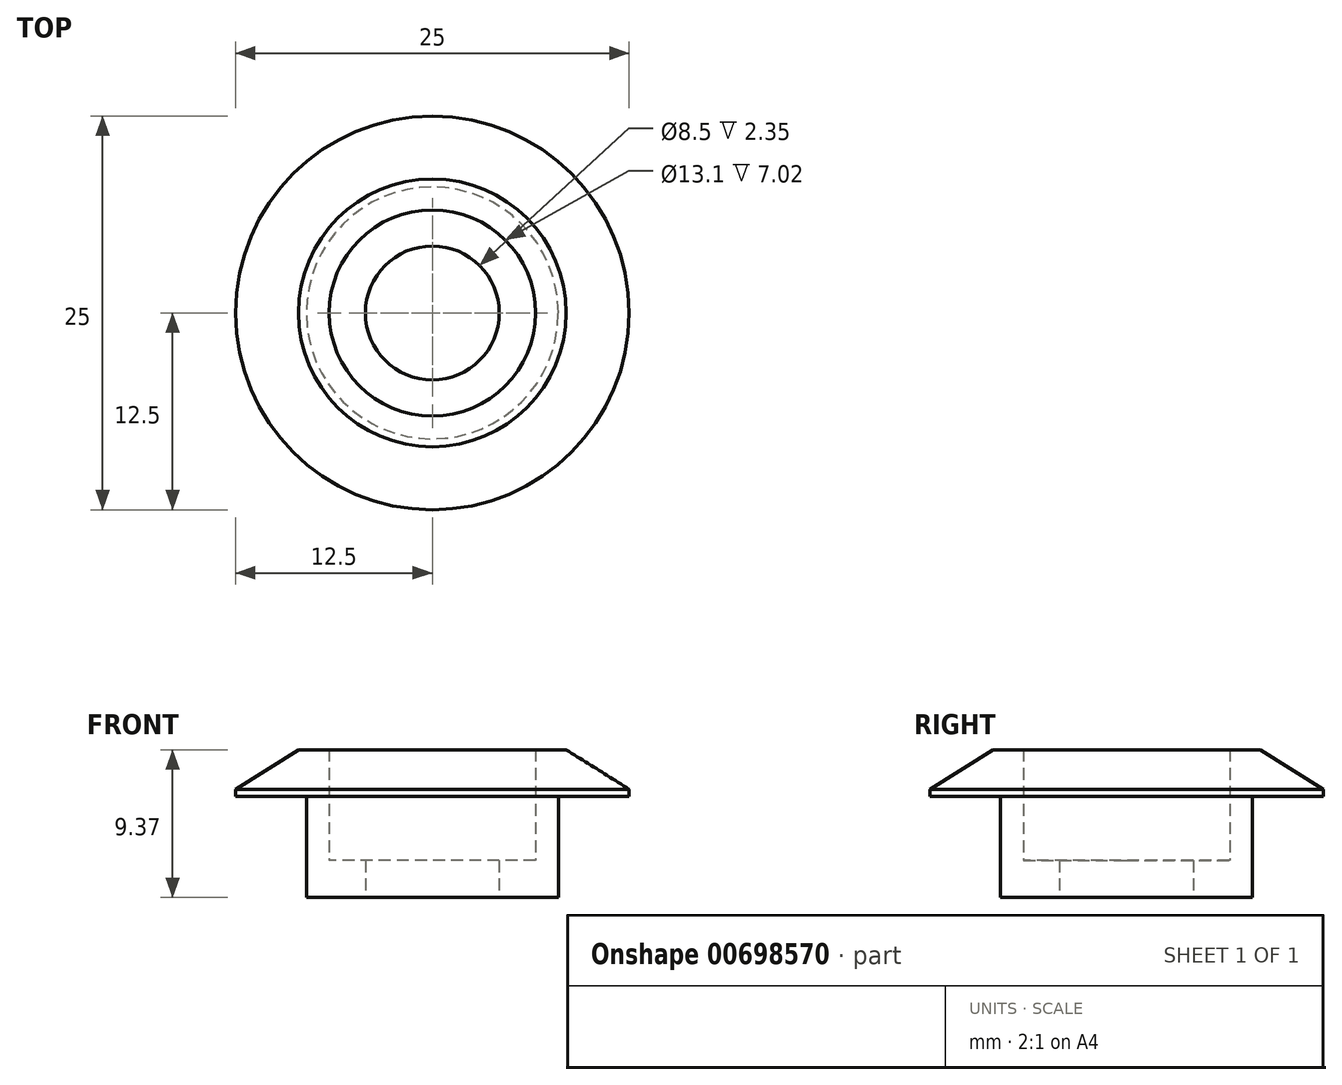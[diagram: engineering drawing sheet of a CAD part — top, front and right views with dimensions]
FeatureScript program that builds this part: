
annotation { "Feature Type Name" : "Feature", "Feature Type Description" : "" }
export const myFeature = defineFeature(function(context is Context, id is Id, definition is map)
    precondition{}
    {
        {
            var Q0;
            Q0=qCreatedBy(makeId("Top.planeOp"),FACE);
            var sketch = newSketch(context, id + "F0", { "sketchPlane" : qUnion([Q0])});
            skCircle(sketch, "E0", {"center": v(0, 0) * mm, "radius": 12.5 * mm});
            skSolve(sketch);
        }
        {
            var Q0;
            Q0 = qSketchRegion(id + "F0", true);
            extrude(context, id + "F1", {"entities" : qUnion([Q0]), "depth" : 9.37 * mm, "offsetDistance" : 25 * mm, "hasSecondDirection" : true, "secondDirectionOppositeDirection" : false, "secondDirectionDepth" : 6.4 * mm});
        }
        {
            var Q0;
            Q0=qCreatedBy(makeId("Top.planeOp"),FACE);
            var sketch = newSketch(context, id + "F2", { "sketchPlane" : qUnion([Q0])});
            skCircle(sketch, "E1", {"center": v(0, 0) * mm, "radius": 8 * mm});
            skSolve(sketch);
        }
        {
            var Q0;
            Q0 = qSketchRegion(id + "F2", true);
            extrude(context, id + "F3", {"entities" : qUnion([Q0]), "operationType" : NewBodyOperationType.ADD, "endBound" : BoundingType.UP_TO_NEXT, "depth" : 25 * mm, "offsetDistance" : 25 * mm});
        }
        {
            var Q0;
            Q0=makeQuery(id+"F1.opExtrude","CAP_EDGE",EDGE,{"disambiguationData":[OSD([sQuery(id+"F0.wireOp",EDGE,"E0")])],"isStart":false});
            chamfer(context, id + "F4", {"entities" : qUnion([Q0]), "chamferType" : ChamferType.TWO_OFFSETS, "width1" : 4 * mm, "oppositeDirection" : false, "width2" : 2.5 * mm, "tangentPropagation" : true});
        }
        {
            var Q0;
            Q0=qCreatedBy(makeId("Top.planeOp"),FACE);
            var sketch = newSketch(context, id + "F5", { "sketchPlane" : qUnion([Q0])});
            skCircle(sketch, "E2", {"center": v(0, 0) * mm, "radius": 4.25 * mm});
            skSolve(sketch);
        }
        {
            var Q0;
            Q0 = qSketchRegion(id + "F5", true);
            extrude(context, id + "F6", {"entities" : qUnion([Q0]), "operationType" : NewBodyOperationType.REMOVE, "endBound" : BoundingType.UP_TO_NEXT, "depth" : 25 * mm, "offsetDistance" : 25 * mm});
        }
        {
            var Q0;
            Q0=qCreatedBy(makeId("Top.planeOp"),FACE);
            var sketch = newSketch(context, id + "F7", { "sketchPlane" : qUnion([Q0])});
            skCircle(sketch, "E3", {"center": v(0, 0) * mm, "radius": 6.55 * mm});
            skSolve(sketch);
        }
        {
            var Q0;
            Q0 = qSketchRegion(id + "F7", true);
            var Q1;
            Q1=makeQuery(id+"F1.opExtrude","CAP_FACE",FACE,{"disambiguationData":[OSD([sQuery(id+"F0.wireOp",EDGE,"E0")])],"isStart":false});
            extrude(context, id + "F8", {"entities" : qUnion([Q0]), "operationType" : NewBodyOperationType.REMOVE, "depth" : 25 * mm, "endBoundEntityFace" : qUnion([Q1]), "offsetDistance" : 25 * mm, "hasSecondDirection" : true, "secondDirectionOppositeDirection" : false, "secondDirectionDepth" : 2.35 * mm});
        }
    });
